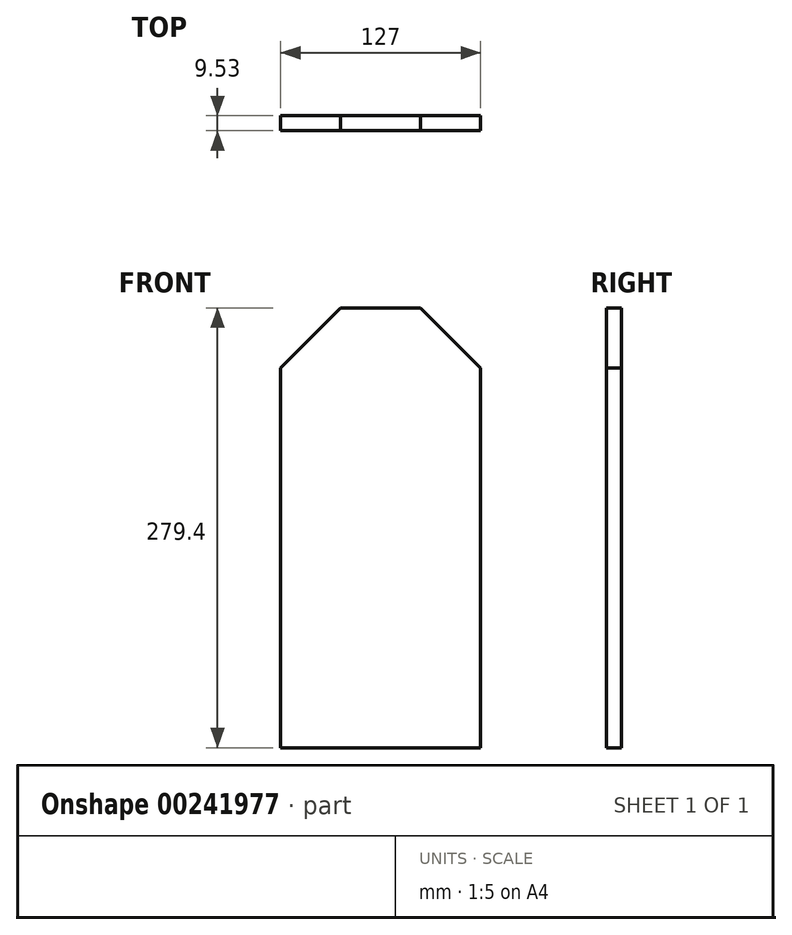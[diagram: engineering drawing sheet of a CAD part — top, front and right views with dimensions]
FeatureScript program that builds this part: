
annotation { "Feature Type Name" : "Feature", "Feature Type Description" : "" }
export const myFeature = defineFeature(function(context is Context, id is Id, definition is map)
    precondition{}
    {
        {
            var Q0;
            Q0=qCreatedBy(makeId("Front.planeOp"),FACE);
            var sketch = newSketch(context, id + "F0", { "sketchPlane" : qUnion([Q0])});
            skLineSegment(sketch, "E0", {"start": v(0, 0) * mm, "end": v(127, 0) * mm});
            skLineSegment(sketch, "E1", {"start": v(127, 0) * mm, "end": v(127, 241.3) * mm});
            skLineSegment(sketch, "E2", {"start": v(127, 241.3) * mm, "end": v(88.9, 279.4) * mm});
            skLineSegment(sketch, "E3", {"start": v(88.9, 279.4) * mm, "end": v(38.1, 279.4) * mm});
            skLineSegment(sketch, "E4", {"start": v(38.1, 279.4) * mm, "end": v(0, 241.3) * mm});
            skLineSegment(sketch, "E5", {"start": v(0, 241.3) * mm, "end": v(0, 0) * mm});
            skSolve(sketch);
        }
        {
            var Q0;
            Q0=makeQuery(id+"F0.imprint","IMPRINT",FACE,{"disambiguationData":[TD([[makeQuery(id+"F0.imprint","IMPRINT",EDGE,{"derivedFrom":sQuery(id+"F0.wireOp",EDGE,"E0")}),1.0]])]});
            extrude(context, id + "F1", {"entities" : qUnion([Q0]), "depth" : 9.52 * mm});
        }
    });
